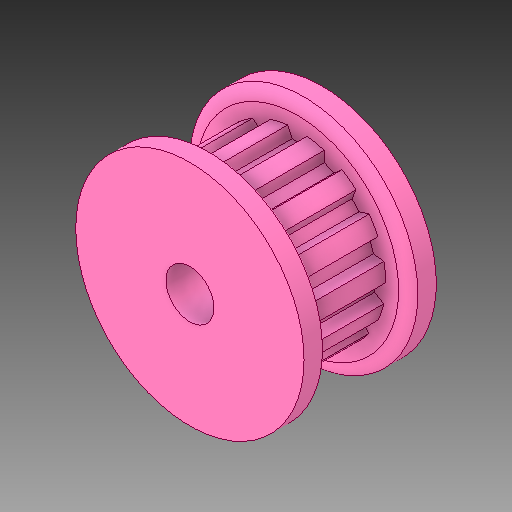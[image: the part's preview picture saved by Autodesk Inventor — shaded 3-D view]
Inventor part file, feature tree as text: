
AUTODESK INVENTOR PART (.ipt)
format: ipt  version: 2017 SP1 (Build 210196100, 196)  size: 253,440 bytes
history: native  units: in
note: dims shown in document units (in); Inventor stores cm internally (conversion verified against a paired STEP export)
features: extrude x3, sketch x3, projected_geometry x3, pattern_circular x1
ambient origin geometry x8: Origin, YZ Plane, XZ Plane, XY Plane, X Axis, Y Axis, Z Axis, Center Point
bodies: Solid1 (feature_tree)
feature tree (10):
  extrude  "Extrusion1"  Depth=1.0in TaperAngle=0.0deg
  extrude  "Extrusion2"  [1 undecoded]
  extrude  "Extrusion3"  [1 undecoded]
  sketch  "Sketch1"  dims[d0=1.0in d1=0.0in d2=0.0625in d3=0.0in]
  projected_geometry  "Projected Loop1"
  sketch  "Sketch2"  dims[d4=0.0625in d5=0.0in]
  projected_geometry  "Projected Loop2"
  sketch  "Sketch3"
  projected_geometry  "Projected Loop3"
  pattern_circular  "CirPattern2"
note: 2 required parameter values undecoded (feature->parameter linkage not recoverable at this tier; creation-order binding heuristic only, values carry confidence <= 0.55)
